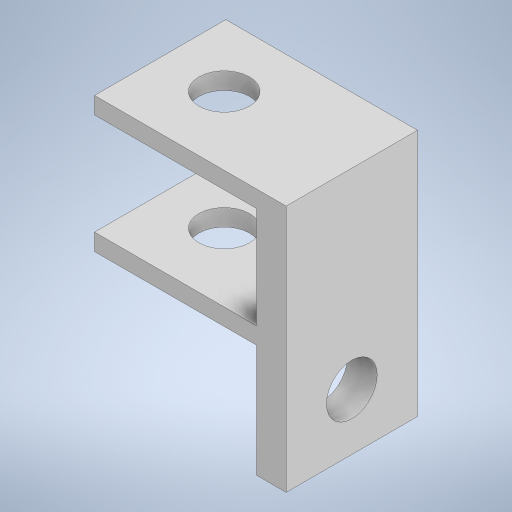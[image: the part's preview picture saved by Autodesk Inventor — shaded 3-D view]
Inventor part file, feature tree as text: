
AUTODESK INVENTOR PART (.ipt)
format: ipt  version: 2024.1 (Build 281209000, 209)  size: 253,440 bytes
history: native  units: mm
features: extrude x5, sketch x5
ambient origin geometry x8: Origin, YZ Plane, XZ Plane, XY Plane, X Axis, Y Axis, Z Axis, Center Point
bodies: Solid1 (feature_tree)
feature tree (10):
  extrude  "Extrusion1"  Depth=11.65mm
  extrude  "Extrusion2"  Depth=9.0mm
  extrude  "Extrusion3"  Depth=1.5mm
  extrude  "Extrusion4"  Depth=4.5mm
  extrude  "Extrusion5"  Depth=10.0mm
  sketch  "Sketch1"  dims[d0=12.0mm d1=11.65mm]
  sketch  "Sketch3"  dims[d2=17.0mm d3=0.0mm d7=9.0mm]
  sketch  "Sketch5"  dims[d8=15.0mm d10=1.5mm]
  sketch  "Sketch6"  dims[d11=14.0mm d12=0.0mm d16=4.5mm]
  sketch  "Sketch7"  dims[d17=8.9mm d18=5.6mm d19=14.0mm d20=0.0mm d21=10.0mm d22=0.0mm d23=5.825mm d24=4.5mm d25=5.0mm d26=4.0mm d27=0.0mm d13=0.5mm d14=0.872665mm]
